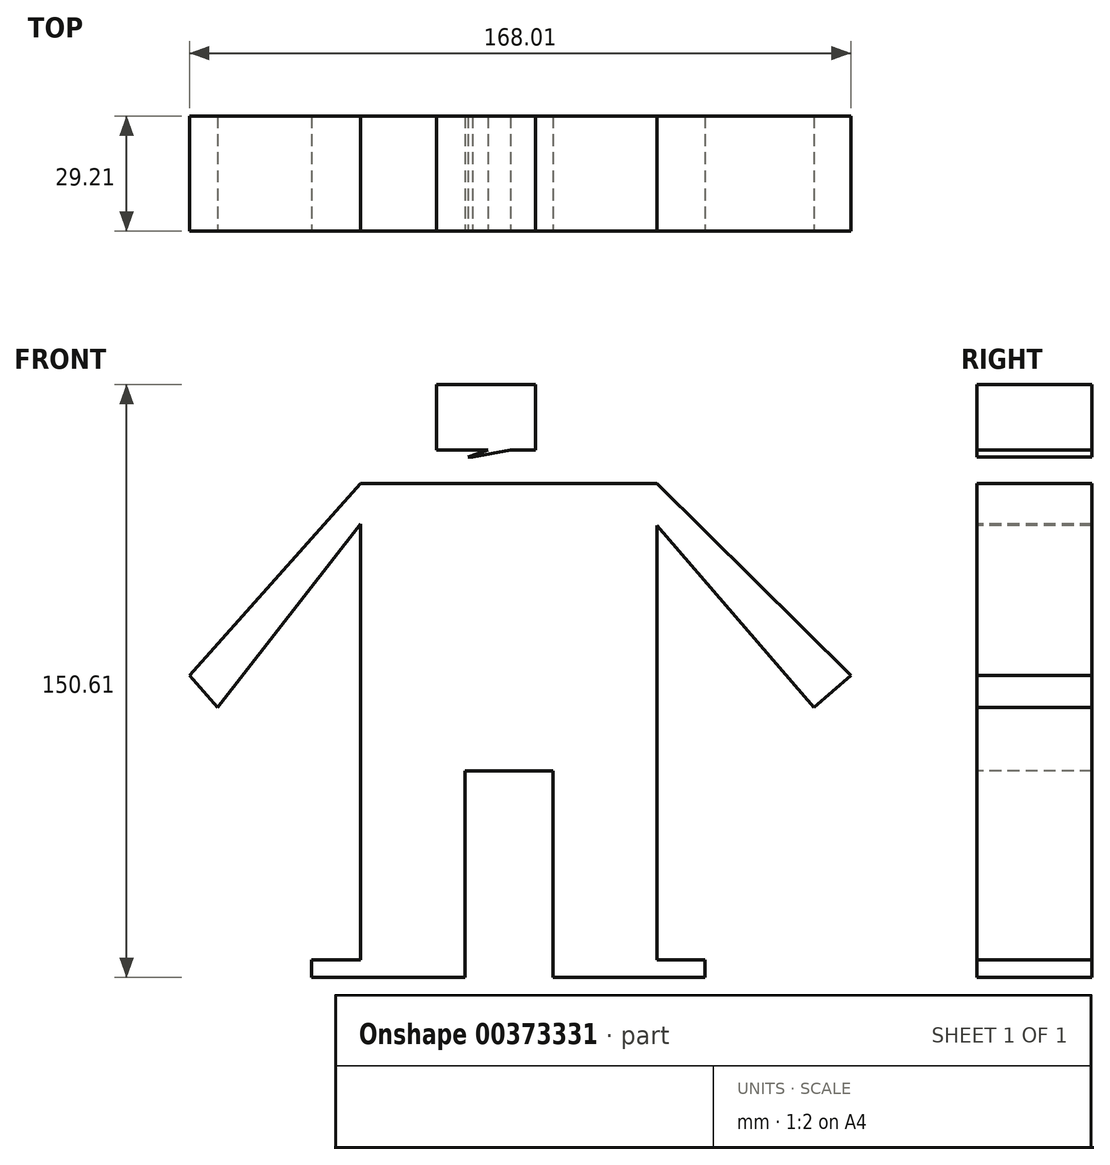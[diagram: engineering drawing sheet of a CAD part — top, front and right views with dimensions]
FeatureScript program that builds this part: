
annotation { "Feature Type Name" : "Feature", "Feature Type Description" : "" }
export const myFeature = defineFeature(function(context is Context, id is Id, definition is map)
    precondition{}
    {
        {
            var Q0;
            Q0=qCreatedBy(makeId("Front.planeOp"),FACE);
            var sketch = newSketch(context, id + "F0", { "sketchPlane" : qUnion([Q0])});
            skLineSegment(sketch, "E0", {"start": v(-60.51, -68.36) * mm, "end": v(-34.07, -68.36) * mm});
            skLineSegment(sketch, "E1", {"start": v(-60.51, -68.36) * mm, "end": v(-60.51, -20.4) * mm});
            skLineSegment(sketch, "E2", {"start": v(-60.51, -20.4) * mm, "end": v(-34.07, -20.4) * mm});
            skLineSegment(sketch, "E3", {"start": v(-34.07, -20.4) * mm, "end": v(-34.07, -72.84) * mm});
            skLineSegment(sketch, "E4", {"start": v(-11.65, -20.4) * mm, "end": v(-11.65, -68.36) * mm});
            skLineSegment(sketch, "E5", {"start": v(-11.65, -68.36) * mm, "end": v(14.8, -68.36) * mm});
            skLineSegment(sketch, "E6", {"start": v(14.8, -68.36) * mm, "end": v(14.8, -20.4) * mm});
            skLineSegment(sketch, "E7", {"start": v(14.8, -20.4) * mm, "end": v(-11.65, -20.4) * mm});
            skLineSegment(sketch, "E8", {"start": v(-34.07, -72.84) * mm, "end": v(-52.9, -72.84) * mm});
            skLineSegment(sketch, "E9", {"start": v(-52.9, -72.84) * mm, "end": v(-73.06, -72.84) * mm});
            skLineSegment(sketch, "E10", {"start": v(-73.06, -72.84) * mm, "end": v(-73.06, -68.36) * mm});
            skLineSegment(sketch, "E11", {"start": v(-73.06, -68.36) * mm, "end": v(-60.51, -68.36) * mm});
            skLineSegment(sketch, "E12", {"start": v(-11.65, -68.36) * mm, "end": v(-11.65, -72.84) * mm});
            skLineSegment(sketch, "E13", {"start": v(-11.65, -72.84) * mm, "end": v(6.72, -72.84) * mm});
            skLineSegment(sketch, "E14", {"start": v(6.72, -72.84) * mm, "end": v(26.9, -72.84) * mm});
            skLineSegment(sketch, "E15", {"start": v(26.9, -72.84) * mm, "end": v(26.9, -68.36) * mm});
            skLineSegment(sketch, "E16", {"start": v(26.9, -68.36) * mm, "end": v(14.8, -68.36) * mm});
            skLineSegment(sketch, "E17", {"start": v(-34.07, -20.4) * mm, "end": v(-11.65, -20.4) * mm});
            skLineSegment(sketch, "E18", {"start": v(14.8, -20.4) * mm, "end": v(14.8, -8.74) * mm});
            skLineSegment(sketch, "E19", {"start": v(14.8, -8.74) * mm, "end": v(-60.51, -8.74) * mm});
            skLineSegment(sketch, "E20", {"start": v(-60.51, -8.74) * mm, "end": v(-60.51, -20.4) * mm});
            skLineSegment(sketch, "E21", {"start": v(-60.51, -8.74) * mm, "end": v(-60.51, 42.36) * mm});
            skLineSegment(sketch, "E22", {"start": v(14.8, -8.74) * mm, "end": v(14.8, 41.91) * mm});
            skLineSegment(sketch, "E23", {"start": v(-60.51, 42.36) * mm, "end": v(-96.82, -4.26) * mm});
            skLineSegment(sketch, "E24", {"start": v(-104, 3.81) * mm, "end": v(-96.82, -4.26) * mm});
            skLineSegment(sketch, "E25", {"start": v(-104, 3.81) * mm, "end": v(-60.51, 52.67) * mm});
            skLineSegment(sketch, "E26", {"start": v(14.8, 41.91) * mm, "end": v(54.69, -4.26) * mm});
            skLineSegment(sketch, "E27", {"start": v(54.69, -4.26) * mm, "end": v(64.02, 3.81) * mm});
            skLineSegment(sketch, "E28", {"start": v(64.02, 3.81) * mm, "end": v(14.8, 52.67) * mm});
            skLineSegment(sketch, "E29", {"start": v(-60.51, 52.67) * mm, "end": v(14.8, 52.67) * mm});
            skLineSegment(sketch, "E30", {"start": v(-45.27, 52.67) * mm, "end": v(-5.83, 52.67) * mm});
            skLineSegment(sketch, "E31", {"start": v(-34.07, 52.67) * mm, "end": v(-34.07, 59.4) * mm});
            skLineSegment(sketch, "E32", {"start": v(-34.07, 59.4) * mm, "end": v(-22.41, 59.4) * mm});
            skLineSegment(sketch, "E33", {"start": v(-22.41, 59.4) * mm, "end": v(-22.41, 52.67) * mm});
            skLineSegment(sketch, "E34", {"start": v(-22.41, 52.67) * mm, "end": v(-22.41, 59.4) * mm});
            skLineSegment(sketch, "E35", {"start": v(-22.41, 61.18) * mm, "end": v(-16.14, 61.18) * mm});
            skLineSegment(sketch, "E36", {"start": v(-16.14, 61.18) * mm, "end": v(-16.14, 77.77) * mm});
            skLineSegment(sketch, "E37", {"start": v(-16.14, 77.77) * mm, "end": v(-41.24, 77.77) * mm});
            skLineSegment(sketch, "E38", {"start": v(-41.24, 77.77) * mm, "end": v(-41.24, 61.18) * mm});
            skLineSegment(sketch, "E39", {"start": v(-41.24, 61.18) * mm, "end": v(-28.24, 61.18) * mm});
            skPoint(sketch, "E39.endSnap0", {"position": v(-28.24, 59.4) * mm});
            skLineSegment(sketch, "E40", {"start": v(-28.24, 61.18) * mm, "end": v(-34.51, 58.94) * mm});
            skLineSegment(sketch, "E41", {"start": v(-34.51, 58.94) * mm, "end": v(-22.41, 61.18) * mm});
            skLineSegment(sketch, "E42", {"start": v(-32.72, 73.29) * mm, "end": v(-28.24, 73.29) * mm});
            skLineSegment(sketch, "E43", {"start": v(-34.07, 61.18) * mm, "end": v(-22.41, 66.12) * mm});
            skSolve(sketch);
        }
        {
            var Q0;
            Q0=makeQuery(id+"F0.imprint","IMPRINT",FACE,{"disambiguationData":[TD([[makeQuery(id+"F0.imprint","IMPRINT",EDGE,{"derivedFrom":sQuery(id+"F0.wireOp",EDGE,"E19")}),-1.0]])]});
            var Q1;
            {var subQ0=sQuery(id+"F0.wireOp",EDGE,"E0");Q1=makeQuery(id+"F0.imprint","IMPRINT",FACE,{"disambiguationData":[TD([[makeQuery(id+"F0.imprint","IMPRINT",EDGE,{"derivedFrom":subQ0}),1.0]])]});}
            var Q2;
            Q2=makeQuery(id+"F0.imprint","IMPRINT",FACE,{"disambiguationData":[TD([[makeQuery(id+"F0.imprint","IMPRINT",EDGE,{"derivedFrom":sQuery(id+"F0.wireOp",EDGE,"E4")}),1.0]])]});
            var Q3;
            Q3=makeQuery(id+"F0.imprint","IMPRINT",FACE,{"disambiguationData":[TD([[makeQuery(id+"F0.imprint","IMPRINT",EDGE,{"derivedFrom":sQuery(id+"F0.wireOp",EDGE,"E2")}),1.0]])]});
            var Q4;
            Q4=makeQuery(id+"F0.imprint","IMPRINT",FACE,{"disambiguationData":[TD([[makeQuery(id+"F0.imprint","IMPRINT",EDGE,{"derivedFrom":sQuery(id+"F0.wireOp",EDGE,"E5")}),-1.0]])]});
            var Q5;
            {var subQ2=sQuery(id+"F0.wireOp",EDGE,"E0");Q5=makeQuery(id+"F0.imprint","IMPRINT",FACE,{"disambiguationData":[TD([[makeQuery(id+"F0.imprint","IMPRINT",EDGE,{"derivedFrom":subQ2}),-1.0]])]});}
            var Q6;
            {var subQ0=sQuery(id+"F0.wireOp",EDGE,"E35");Q6=makeQuery(id+"F0.imprint","IMPRINT",FACE,{"disambiguationData":[TD([[makeQuery(id+"F0.imprint","IMPRINT",EDGE,{"derivedFrom":subQ0}),1.0]])]});}
            var Q7;
            {var subQ0=sQuery(id+"F0.wireOp",EDGE,"E34");Q7=makeQuery(id+"F0.imprint","IMPRINT",FACE,{"disambiguationData":[TD([[makeQuery(id+"F0.imprint","IMPRINT",EDGE,{"derivedFrom":subQ0}),1.0]])]});}
            extrude(context, id + "F1", {"entities" : qUnion([Q0, Q1, Q2, Q3, Q4, Q5, Q6, Q7]), "oppositeDirection" : true, "depth" : 3.8 * mm});
        }
        {
            var Q0;
            Q0=makeQuery(id+"F1.opExtrude","CAP_FACE",FACE,{"disambiguationData":[OSD([sQuery(id+"F0.wireOp",EDGE,"E1"),sQuery(id+"F0.wireOp",EDGE,"E3"),sQuery(id+"F0.wireOp",EDGE,"E4"),sQuery(id+"F0.wireOp",EDGE,"E6"),sQuery(id+"F0.wireOp",EDGE,"E8"),sQuery(id+"F0.wireOp",EDGE,"E9"),sQuery(id+"F0.wireOp",EDGE,"E10"),sQuery(id+"F0.wireOp",EDGE,"E11"),sQuery(id+"F0.wireOp",EDGE,"E12"),sQuery(id+"F0.wireOp",EDGE,"E13"),sQuery(id+"F0.wireOp",EDGE,"E14"),sQuery(id+"F0.wireOp",EDGE,"E15"),sQuery(id+"F0.wireOp",EDGE,"E16"),sQuery(id+"F0.wireOp",EDGE,"E17"),sQuery(id+"F0.wireOp",EDGE,"E18"),sQuery(id+"F0.wireOp",EDGE,"E20"),sQuery(id+"F0.wireOp",EDGE,"E21"),sQuery(id+"F0.wireOp",EDGE,"E22"),sQuery(id+"F0.wireOp",EDGE,"E23"),sQuery(id+"F0.wireOp",EDGE,"E24"),sQuery(id+"F0.wireOp",EDGE,"E25"),sQuery(id+"F0.wireOp",EDGE,"E26"),sQuery(id+"F0.wireOp",EDGE,"E27"),sQuery(id+"F0.wireOp",EDGE,"E28"),sQuery(id+"F0.wireOp",EDGE,"E29"),sQuery(id+"F0.wireOp",EDGE,"E30"),sQuery(id+"F0.wireOp",EDGE,"E31"),sQuery(id+"F0.wireOp",EDGE,"E32"),sQuery(id+"F0.wireOp",EDGE,"E34"),sQuery(id+"F0.wireOp",EDGE,"E41")])],"isStart":true});
            extrude(context, id + "F2", {"entities" : qUnion([Q0]), "operationType" : NewBodyOperationType.ADD, "depth" : 25.4 * mm});
        }
        {
            var Q0;
            Q0=makeQuery(id+"F1.opExtrude","CAP_FACE",FACE,{"disambiguationData":[OSD([sQuery(id+"F0.wireOp",EDGE,"E32"),sQuery(id+"F0.wireOp",EDGE,"E35"),sQuery(id+"F0.wireOp",EDGE,"E36"),sQuery(id+"F0.wireOp",EDGE,"E37"),sQuery(id+"F0.wireOp",EDGE,"E38"),sQuery(id+"F0.wireOp",EDGE,"E39"),sQuery(id+"F0.wireOp",EDGE,"E40"),sQuery(id+"F0.wireOp",EDGE,"E41")])],"isStart":true});
            extrude(context, id + "F3", {"entities" : qUnion([Q0]), "operationType" : NewBodyOperationType.ADD, "depth" : 25.4 * mm});
        }
    });
